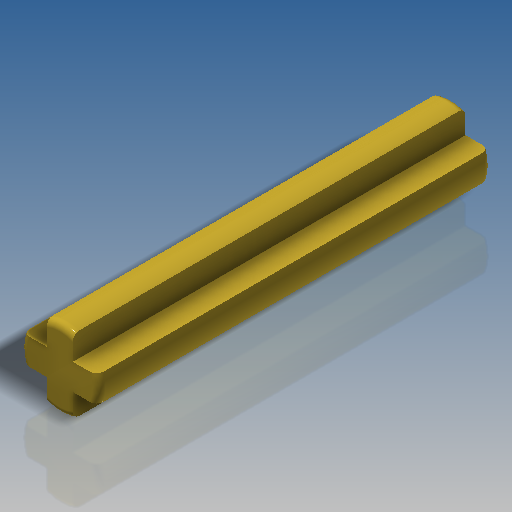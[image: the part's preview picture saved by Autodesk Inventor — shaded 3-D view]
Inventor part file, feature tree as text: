
AUTODESK INVENTOR PART (.ipt)
format: ipt  version: 2019.4 (Build 234330000, 330)  size: 193,024 bytes
history: native  units: in
note: dims shown in document units (in); Inventor stores cm internally (conversion verified against a paired STEP export)
features: extrude x1, fillet x1, sketch x1
ambient origin geometry x8: Origin, YZ Plane, XZ Plane, XY Plane, X Axis, Y Axis, Z Axis, Center Point
bodies: Solid1 (feature_tree)
feature tree (3):
  extrude  "Extrusion1"  Depth=0.0157in
  fillet  "Fillet1"  Radius=0.9449in
  sketch  "Sketch1"  dims[d0=0.189in d1=0.063in d2=0.9449in d3=0.0in d4=0.0157in d5=0.0in d6=0.0in]
